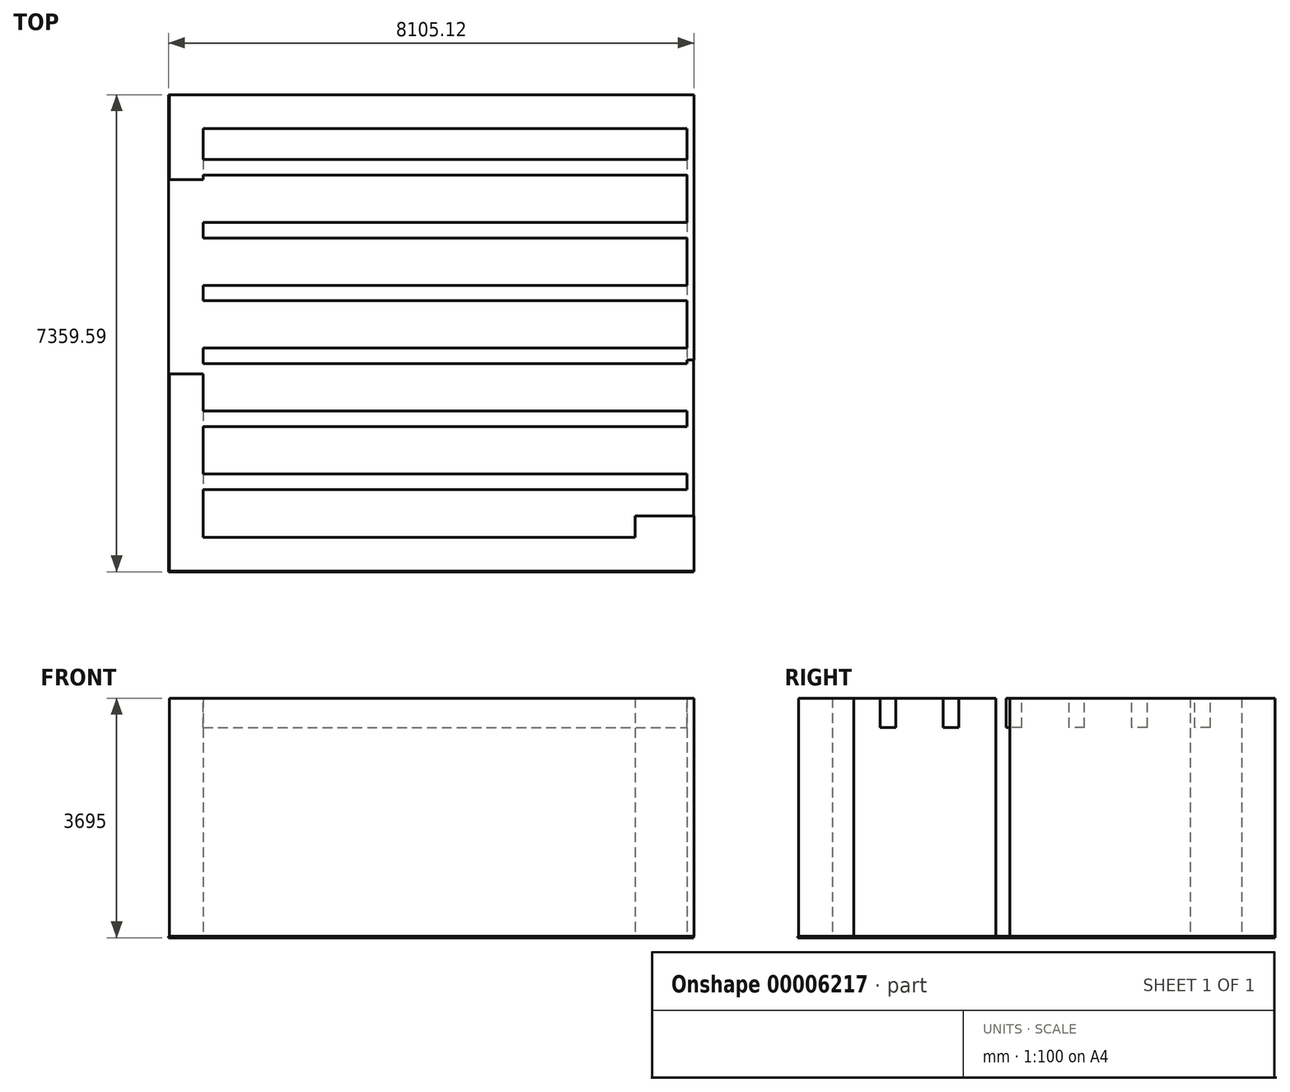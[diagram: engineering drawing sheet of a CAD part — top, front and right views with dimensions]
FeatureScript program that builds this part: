
annotation { "Feature Type Name" : "Feature", "Feature Type Description" : "" }
export const myFeature = defineFeature(function(context is Context, id is Id, definition is map)
    precondition{}
    {
        {
            var Q0;
            Q0=qCreatedBy(makeId("Top.planeOp"),FACE);
            var sketch = newSketch(context, id + "F0", { "sketchPlane" : qUnion([Q0])});
            skLineSegment(sketch, "E0.rect.bottom", {"start": v(3730, 3155) * mm, "end": v(-3730, 3155) * mm});
            skLineSegment(sketch, "E0.rect.top", {"start": v(3730, -3155) * mm, "end": v(-3730, -3155) * mm});
            skLineSegment(sketch, "E0.rect.left", {"start": v(3730, 3155) * mm, "end": v(3730, -415) * mm});
            skLineSegment(sketch, "E0.rect.right", {"start": v(-3730, 3155) * mm, "end": v(-3730, 2365) * mm});
            skPoint(sketch, "E0.rect.middle", {"position": v(0, 0) * mm});
            skLineSegment(sketch, "E1.0", {"start": v(3840, 3675) * mm, "end": v(-4250, 3675) * mm});
            skLineSegment(sketch, "E1.2", {"start": v(3840, -3675) * mm, "end": v(-4250, -3675) * mm});
            skLineSegment(sketch, "E1.3", {"start": v(-4250, 3675) * mm, "end": v(-4250, 2365) * mm});
            skLineSegment(sketch, "E2.bottom", {"start": v(-4250, 2365) * mm, "end": v(-3730, 2365) * mm});
            skLineSegment(sketch, "E2.top", {"start": v(-4250, -635) * mm, "end": v(-3730, -635) * mm});
            skLineSegment(sketch, "E3.trimOffspring", {"start": v(-3730, -635) * mm, "end": v(-3730, -3155) * mm});
            skLineSegment(sketch, "E4.trimOffspring", {"start": v(-4250, -635) * mm, "end": v(-4250, -3675) * mm});
            skLineSegment(sketch, "E5.bottom", {"start": v(3730, -3155) * mm, "end": v(2930, -3155) * mm});
            skLineSegment(sketch, "E5.top", {"start": v(3730, -2825) * mm, "end": v(2930, -2825) * mm});
            skLineSegment(sketch, "E5.left", {"start": v(3730, -3155) * mm, "end": v(3730, -2825) * mm});
            skLineSegment(sketch, "E5.right", {"start": v(2930, -3155) * mm, "end": v(2930, -2825) * mm});
            skLineSegment(sketch, "E6.bottom", {"start": v(3730, -2825) * mm, "end": v(3840, -2825) * mm});
            skLineSegment(sketch, "E6.top", {"start": v(3730, -415) * mm, "end": v(3840, -415) * mm});
            skLineSegment(sketch, "E7.right", {"start": v(3840, 3675) * mm, "end": v(3840, -415) * mm});
            skLineSegment(sketch, "E8.trimOffspring", {"start": v(3840, -2825) * mm, "end": v(3840, -3675) * mm});
            skLineSegment(sketch, "E9.trimOffspring", {"start": v(3730, -2825) * mm, "end": v(3730, -3155) * mm});
            skSolve(sketch);
        }
        {
            var Q0;
            Q0 = qSketchRegion(id + "F0", true);
            extrude(context, id + "F1", {"entities" : qUnion([Q0]), "depth" : 3670 * mm});
        }
        {
            var Q0;
            Q0=qCreatedBy(makeId("Top.planeOp"),FACE);
            var sketch = newSketch(context, id + "F2", { "sketchPlane" : qUnion([Q0])});
            skLineSegment(sketch, "E10.bottom", {"start": v(-4265.12, -3684.59) * mm, "end": v(3833.35, -3684.59) * mm});
            skLineSegment(sketch, "E10.top", {"start": v(-4265.12, 3673.7) * mm, "end": v(3833.35, 3673.7) * mm});
            skLineSegment(sketch, "E10.left", {"start": v(-4265.12, -3684.59) * mm, "end": v(-4265.12, 3673.7) * mm});
            skLineSegment(sketch, "E10.right", {"start": v(3833.35, -3684.59) * mm, "end": v(3833.35, 3673.7) * mm});
            skSolve(sketch);
        }
        {
            var Q0;
            Q0 = qSketchRegion(id + "F2", true);
            extrude(context, id + "F3", {"entities" : qUnion([Q0]), "operationType" : NewBodyOperationType.ADD, "oppositeDirection" : true, "depth" : 25 * mm});
        }
        {
            var Q0;
            Q0=makeQuery(id+"F1.opExtrude","CAP_FACE",FACE,{"disambiguationData":[OSD([sQuery(id+"F0.wireOp",EDGE,"E0.rect.bottom"),sQuery(id+"F0.wireOp",EDGE,"E0.rect.left"),sQuery(id+"F0.wireOp",EDGE,"E0.rect.right"),sQuery(id+"F0.wireOp",EDGE,"E1.0"),sQuery(id+"F0.wireOp",EDGE,"E1.3"),sQuery(id+"F0.wireOp",EDGE,"E2.bottom"),sQuery(id+"F0.wireOp",EDGE,"E6.top"),sQuery(id+"F0.wireOp",EDGE,"E7.right")])],"isStart":false});
            var sketch = newSketch(context, id + "F4", { "sketchPlane" : qUnion([Q0])});
            skLineSegment(sketch, "E11.bottom", {"start": v(-3730, 3155) * mm, "end": v(3730, 3155) * mm, "construction": true});
            skLineSegment(sketch, "E11.top", {"start": v(-3730, -3145) * mm, "end": v(3730, -3145) * mm, "construction": true});
            skLineSegment(sketch, "E11.left", {"start": v(-3730, 3155) * mm, "end": v(-3730, -3145) * mm, "construction": true});
            skLineSegment(sketch, "E11.right", {"start": v(3730, 3155) * mm, "end": v(3730, -3145) * mm, "construction": true});
            skLineSegment(sketch, "E12.top", {"start": v(-3730, 2675) * mm, "end": v(3730, 2675) * mm});
            skLineSegment(sketch, "E12.left", {"start": v(-3730, 3155) * mm, "end": v(-3730, 2675) * mm, "construction": true});
            skLineSegment(sketch, "E12.right", {"start": v(3730, 3155) * mm, "end": v(3730, 2675) * mm, "construction": true});
            skLineSegment(sketch, "E13.bottom", {"start": v(-3730, 2435) * mm, "end": v(3730, 2435) * mm});
            skLineSegment(sketch, "E13.top", {"start": v(-3730, 1705) * mm, "end": v(3730, 1705) * mm});
            skLineSegment(sketch, "E13.left", {"start": v(-3730, 2435) * mm, "end": v(-3730, 1705) * mm, "construction": true});
            skLineSegment(sketch, "E13.right", {"start": v(3730, 2435) * mm, "end": v(3730, 1705) * mm, "construction": true});
            skLineSegment(sketch, "E14.bottom", {"start": v(-3730, 1465) * mm, "end": v(3730, 1465) * mm});
            skLineSegment(sketch, "E14.top", {"start": v(-3730, 735) * mm, "end": v(3730, 735) * mm});
            skLineSegment(sketch, "E14.left", {"start": v(-3730, 1465) * mm, "end": v(-3730, 735) * mm, "construction": true});
            skLineSegment(sketch, "E14.right", {"start": v(3730, 1465) * mm, "end": v(3730, 735) * mm, "construction": true});
            skLineSegment(sketch, "E15.bottom", {"start": v(-3730, 495) * mm, "end": v(3730, 495) * mm});
            skLineSegment(sketch, "E15.top", {"start": v(-3730, -235) * mm, "end": v(3730, -235) * mm});
            skLineSegment(sketch, "E15.left", {"start": v(-3730, 495) * mm, "end": v(-3730, -235) * mm, "construction": true});
            skLineSegment(sketch, "E15.right", {"start": v(3730, 495) * mm, "end": v(3730, -235) * mm, "construction": true});
            skLineSegment(sketch, "E16.bottom", {"start": v(-3730, -475) * mm, "end": v(3730, -475) * mm});
            skLineSegment(sketch, "E16.top", {"start": v(-3730, -1205) * mm, "end": v(3730, -1205) * mm});
            skLineSegment(sketch, "E16.left", {"start": v(-3730, -475) * mm, "end": v(-3730, -1205) * mm, "construction": true});
            skLineSegment(sketch, "E16.right", {"start": v(3730, -475) * mm, "end": v(3730, -1205) * mm, "construction": true});
            skLineSegment(sketch, "E17.bottom", {"start": v(3730, -1445) * mm, "end": v(-3730, -1445) * mm});
            skLineSegment(sketch, "E17.top", {"start": v(3730, -2175) * mm, "end": v(-3730, -2175) * mm});
            skLineSegment(sketch, "E17.left", {"start": v(3730, -1445) * mm, "end": v(3730, -2175) * mm, "construction": true});
            skLineSegment(sketch, "E17.right", {"start": v(-3730, -1445) * mm, "end": v(-3730, -2175) * mm, "construction": true});
            skLineSegment(sketch, "E18.bottom", {"start": v(-3730, -2415) * mm, "end": v(3730, -2415) * mm});
            skLineSegment(sketch, "E18.left", {"start": v(-3730, -2415) * mm, "end": v(-3730, -3145) * mm, "construction": true});
            skLineSegment(sketch, "E18.right", {"start": v(3730, -2415) * mm, "end": v(3730, -3145) * mm, "construction": true});
            skLineSegment(sketch, "E19", {"start": v(-3730, 2675) * mm, "end": v(-3730, 2435) * mm});
            skLineSegment(sketch, "E20", {"start": v(-3730, 1705) * mm, "end": v(-3730, 1465) * mm});
            skLineSegment(sketch, "E21", {"start": v(-3730, 735) * mm, "end": v(-3730, 495) * mm});
            skLineSegment(sketch, "E22", {"start": v(-3730, -235) * mm, "end": v(-3730, -475) * mm});
            skLineSegment(sketch, "E23", {"start": v(-3730, -1205) * mm, "end": v(-3730, -1445) * mm});
            skLineSegment(sketch, "E24", {"start": v(-3730, -2175) * mm, "end": v(-3730, -2415) * mm});
            skLineSegment(sketch, "E25", {"start": v(3730, 2675) * mm, "end": v(3730, 2435) * mm});
            skLineSegment(sketch, "E26", {"start": v(3730, 1705) * mm, "end": v(3730, 1465) * mm});
            skLineSegment(sketch, "E27", {"start": v(3730, 735) * mm, "end": v(3730, 495) * mm});
            skLineSegment(sketch, "E28", {"start": v(3730, -235) * mm, "end": v(3730, -475) * mm});
            skLineSegment(sketch, "E29", {"start": v(3730, -1205) * mm, "end": v(3730, -1445) * mm});
            skLineSegment(sketch, "E30", {"start": v(3730, -2175) * mm, "end": v(3730, -2415) * mm});
            skSolve(sketch);
        }
        {
            var Q0;
            Q0 = qSketchRegion(id + "F4", true);
            extrude(context, id + "F5", {"entities" : qUnion([Q0]), "operationType" : NewBodyOperationType.ADD, "oppositeDirection" : true, "depth" : 450 * mm});
        }
    });
